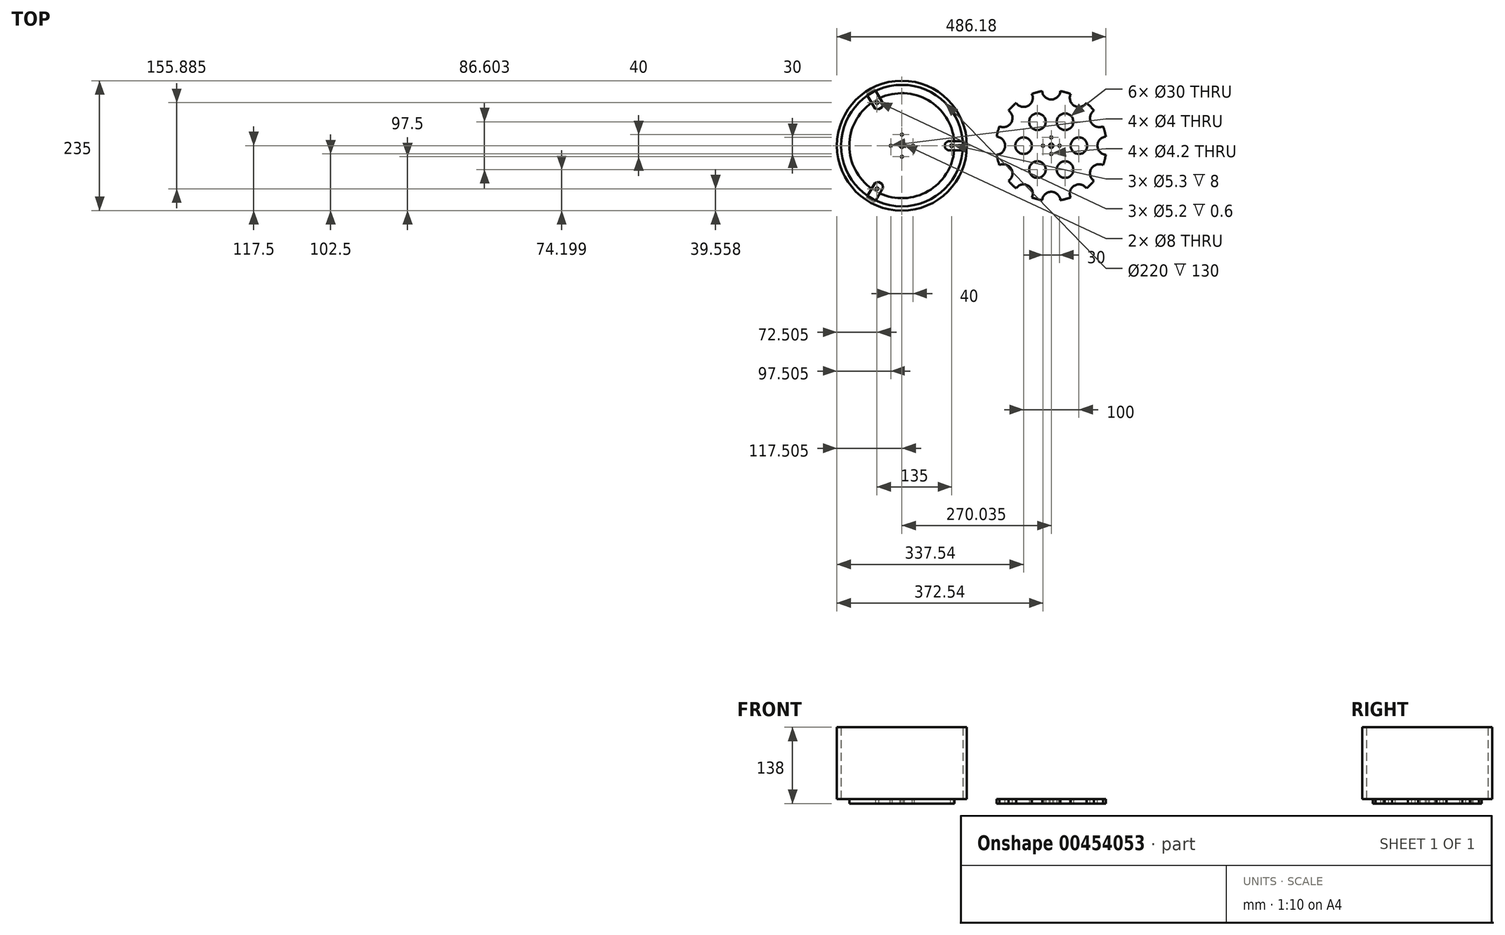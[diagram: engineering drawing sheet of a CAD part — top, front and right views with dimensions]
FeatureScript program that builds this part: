
annotation { "Feature Type Name" : "Feature", "Feature Type Description" : "" }
export const myFeature = defineFeature(function(context is Context, id is Id, definition is map)
    precondition{}
    {
        {
            var Q0;
            Q0=qCreatedBy(makeId("Top.planeOp"),FACE);
            var sketch = newSketch(context, id + "F0", { "sketchPlane" : qUnion([Q0])});
            skCircle(sketch, "E0", {"center": v(0, 0) * mm, "radius": 100 * mm});
            skCircle(sketch, "E1", {"center": v(0, 15) * mm, "radius": 2.1 * mm});
            skCircle(sketch, "E2.1.0", {"center": v(-15, 0) * mm, "radius": 2.1 * mm});
            skCircle(sketch, "E2.2.0", {"center": v(0, -15) * mm, "radius": 2.1 * mm});
            skCircle(sketch, "E2.3.0", {"center": v(15, 0) * mm, "radius": 2.1 * mm});
            skCircle(sketch, "E3", {"center": v(0, 0) * mm, "radius": 4 * mm});
            skCircle(sketch, "E4", {"center": v(-50, 0) * mm, "radius": 15 * mm});
            skCircle(sketch, "E5.1.0", {"center": v(-25, -43.3) * mm, "radius": 15 * mm});
            skCircle(sketch, "E5.2.0", {"center": v(25, -43.3) * mm, "radius": 15 * mm});
            skCircle(sketch, "E5.3.0", {"center": v(50, 0) * mm, "radius": 15 * mm});
            skCircle(sketch, "E5.4.0", {"center": v(25, 43.3) * mm, "radius": 15 * mm});
            skCircle(sketch, "E6.1.5.0", {"center": v(-25, 43.3) * mm, "radius": 15 * mm});
            skSolve(sketch);
        }
        {
            var Q0;
            Q0 = qSketchRegion(id + "F0", true);
            extrude(context, id + "F1", {"entities" : qUnion([Q0]), "depth" : 8 * mm, "offsetDistance" : 25 * mm});
        }
        {
            var Q0;
            Q0=makeQuery(id+"F1.opExtrude","CAP_FACE",FACE,{"disambiguationData":[OSD([sQuery(id+"F0.wireOp",EDGE,"E0"),sQuery(id+"F0.wireOp",EDGE,"E1"),sQuery(id+"F0.wireOp",EDGE,"E2.1.0"),sQuery(id+"F0.wireOp",EDGE,"E2.2.0"),sQuery(id+"F0.wireOp",EDGE,"E2.3.0")])],"isStart":false});
            var sketch = newSketch(context, id + "F2", { "sketchPlane" : qUnion([Q0])});
            skCircle(sketch, "E7", {"center": v(0, 100) * mm, "radius": 16.5 * mm});
            skCircle(sketch, "E8.1.0", {"center": v(-50, 86.6) * mm, "radius": 16.5 * mm});
            skCircle(sketch, "E8.2.0", {"center": v(-86.6, 50) * mm, "radius": 16.5 * mm});
            skCircle(sketch, "E8.3.0", {"center": v(-100, 0) * mm, "radius": 16.5 * mm});
            skCircle(sketch, "E8.4.0", {"center": v(-86.6, -50) * mm, "radius": 16.5 * mm});
            skCircle(sketch, "E8.5.0", {"center": v(-50, -86.6) * mm, "radius": 16.5 * mm});
            skCircle(sketch, "E8.6.0", {"center": v(0, -100) * mm, "radius": 16.5 * mm});
            skCircle(sketch, "E8.7.0", {"center": v(50, -86.6) * mm, "radius": 16.5 * mm});
            skCircle(sketch, "E8.8.0", {"center": v(86.6, -50) * mm, "radius": 16.5 * mm});
            skCircle(sketch, "E8.9.0", {"center": v(100, 0) * mm, "radius": 16.5 * mm});
            skCircle(sketch, "E8.10.0", {"center": v(86.6, 50) * mm, "radius": 16.5 * mm});
            skCircle(sketch, "E8.11.0", {"center": v(50, 86.6) * mm, "radius": 16.5 * mm});
            skPoint(sketch, "E8.center", {"position": v(0, 0) * mm});
            skSolve(sketch);
        }
        {
            var Q0;
            Q0 = qSketchRegion(id + "F2", true);
            extrude(context, id + "F3", {"entities" : qUnion([Q0]), "operationType" : NewBodyOperationType.REMOVE, "oppositeDirection" : true, "depth" : 8 * mm, "offsetDistance" : 25 * mm});
        }
        {
            var Q0;
            Q0=qCreatedBy(makeId("Top.planeOp"),FACE);
            var sketch = newSketch(context, id + "F4", { "sketchPlane" : qUnion([Q0])});
            skCircle(sketch, "E9", {"center": v(-270.04, 0) * mm, "radius": 95 * mm});
            skCircle(sketch, "E10", {"center": v(-180.04, 0) * mm, "radius": 2.65 * mm});
            skCircle(sketch, "E11.1.0", {"center": v(-315.04, 77.94) * mm, "radius": 2.65 * mm});
            skCircle(sketch, "E11.2.0", {"center": v(-315.04, -77.94) * mm, "radius": 2.65 * mm});
            skCircle(sketch, "E12", {"center": v(-270.04, 0) * mm, "radius": 4 * mm});
            skCircle(sketch, "E13", {"center": v(-270.04, 20) * mm, "radius": 2 * mm});
            skCircle(sketch, "E14.1.0", {"center": v(-290.04, 0) * mm, "radius": 2 * mm});
            skCircle(sketch, "E14.2.0", {"center": v(-270.04, -20) * mm, "radius": 2 * mm});
            skCircle(sketch, "E15.1.3.0", {"center": v(-250.04, 0) * mm, "radius": 2 * mm});
            skSolve(sketch);
        }
        {
            var Q0;
            Q0 = qSketchRegion(id + "F4", true);
            extrude(context, id + "F5", {"entities" : qUnion([Q0]), "depth" : 8 * mm, "offsetDistance" : 25 * mm});
        }
        {
            var Q0;
            Q0=makeQuery(id+"F5.opExtrude","CAP_FACE",FACE,{"disambiguationData":[OSD([sQuery(id+"F4.wireOp",EDGE,"E9"),sQuery(id+"F4.wireOp",EDGE,"E10"),sQuery(id+"F4.wireOp",EDGE,"E11.1.0"),sQuery(id+"F4.wireOp",EDGE,"E11.2.0"),sQuery(id+"F4.wireOp",EDGE,"E12"),sQuery(id+"F4.wireOp",EDGE,"E13"),sQuery(id+"F4.wireOp",EDGE,"E14.1.0"),sQuery(id+"F4.wireOp",EDGE,"E14.2.0"),sQuery(id+"F4.wireOp",EDGE,"E15.1.3.0")])],"isStart":false});
            var sketch = newSketch(context, id + "F6", { "sketchPlane" : qUnion([Q0])});
            skLineSegment(sketch, "E16.bottom", {"start": v(-191.84, -8.85) * mm, "end": v(-156.84, -8.85) * mm});
            skLineSegment(sketch, "E16.top", {"start": v(-191.84, 8.85) * mm, "end": v(-156.84, 8.85) * mm});
            skLineSegment(sketch, "E16.left", {"start": v(-191.84, -8.85) * mm, "end": v(-191.84, 8.85) * mm});
            skLineSegment(sketch, "E16.right", {"start": v(-156.84, -8.85) * mm, "end": v(-156.84, 8.85) * mm});
            skCircle(sketch, "E17", {"center": v(-180.04, 0) * mm, "radius": 2.6 * mm});
            skLineSegment(sketch, "E18.1.0", {"start": v(-301.47, 72.15) * mm, "end": v(-316.8, 63.3) * mm});
            skLineSegment(sketch, "E18.1.1", {"start": v(-316.8, 63.3) * mm, "end": v(-334.3, 93.6) * mm});
            skLineSegment(sketch, "E18.1.2", {"start": v(-301.47, 72.15) * mm, "end": v(-318.97, 102.46) * mm});
            skLineSegment(sketch, "E18.1.3", {"start": v(-318.97, 102.46) * mm, "end": v(-334.3, 93.6) * mm});
            skCircle(sketch, "E18.1.4", {"center": v(-315.04, 77.94) * mm, "radius": 2.6 * mm});
            skLineSegment(sketch, "E18.2.0", {"start": v(-316.8, -63.3) * mm, "end": v(-301.47, -72.15) * mm});
            skLineSegment(sketch, "E18.2.1", {"start": v(-301.47, -72.15) * mm, "end": v(-318.97, -102.46) * mm});
            skLineSegment(sketch, "E18.2.2", {"start": v(-316.8, -63.3) * mm, "end": v(-334.3, -93.6) * mm});
            skLineSegment(sketch, "E18.2.3", {"start": v(-334.3, -93.6) * mm, "end": v(-318.97, -102.46) * mm});
            skCircle(sketch, "E18.2.4", {"center": v(-315.04, -77.94) * mm, "radius": 2.6 * mm});
            skPoint(sketch, "E18.center", {"position": v(-270.04, 0) * mm});
            skSolve(sketch);
        }
        {
            var Q0;
            Q0 = qSketchRegion(id + "F6", true);
            extrude(context, id + "F7", {"entities" : qUnion([Q0]), "operationType" : NewBodyOperationType.ADD, "depth" : 0.6 * mm, "offsetDistance" : 25 * mm});
        }
        {
            var Q0;
            Q0=makeQuery(id+"F7.opExtrude","SWEPT_EDGE",EDGE,{"disambiguationData":[OSD([sQuery(id+"F6.wireOp",EDGE,"E16.bottom"),sQuery(id+"F6.wireOp",EDGE,"E16.left")])]});
            var Q1;
            Q1=makeQuery(id+"F7.opExtrude","SWEPT_EDGE",EDGE,{"disambiguationData":[OSD([sQuery(id+"F6.wireOp",EDGE,"E16.top"),sQuery(id+"F6.wireOp",EDGE,"E16.left")])]});
            var Q2;
            Q2=makeQuery(id+"F7.opExtrude","SWEPT_EDGE",EDGE,{"disambiguationData":[OSD([sQuery(id+"F6.wireOp",EDGE,"E18.2.0"),sQuery(id+"F6.wireOp",EDGE,"E18.2.2")])]});
            var Q3;
            Q3=makeQuery(id+"F7.opExtrude","SWEPT_EDGE",EDGE,{"disambiguationData":[OSD([sQuery(id+"F6.wireOp",EDGE,"E18.2.0"),sQuery(id+"F6.wireOp",EDGE,"E18.2.1")])]});
            var Q4;
            Q4=makeQuery(id+"F7.opExtrude","SWEPT_EDGE",EDGE,{"disambiguationData":[OSD([sQuery(id+"F6.wireOp",EDGE,"E18.1.0"),sQuery(id+"F6.wireOp",EDGE,"E18.1.1")])]});
            var Q5;
            Q5=makeQuery(id+"F7.opExtrude","SWEPT_EDGE",EDGE,{"disambiguationData":[OSD([sQuery(id+"F6.wireOp",EDGE,"E18.1.0"),sQuery(id+"F6.wireOp",EDGE,"E18.1.2")])]});
            chamfer(context, id + "F8", {"entities" : qUnion([Q0, Q1, Q2, Q3, Q4, Q5]), "width" : 5 * mm, "tangentPropagation" : true});
        }
        {
            var Q0;
            {var subQ0=sQuery(id+"F6.wireOp",EDGE,"E16.bottom");Q0=makeQuery(id+"F7.boolean.opBoolean","SPLIT",EDGE,{"disambiguationData":[topologyDisambiguationEdgeConnected([makeQuery(id+"F7.opExtrude","CAP_FACE",FACE,{"disambiguationData":[OSD([subQ0,sQuery(id+"F6.wireOp",EDGE,"E16.top"),sQuery(id+"F6.wireOp",EDGE,"E16.left"),sQuery(id+"F6.wireOp",EDGE,"E16.right"),sQuery(id+"F6.wireOp",EDGE,"E17")])],"isStart":true})])],"derivedFrom":makeQuery(id+"F7.opExtrude","CAP_EDGE",EDGE,{"disambiguationData":[OSD([subQ0])],"isStart":true})});}
            var Q1;
            {var subQ0=sQuery(id+"F6.wireOp",EDGE,"E16.top");Q1=makeQuery(id+"F7.boolean.opBoolean","SPLIT",EDGE,{"disambiguationData":[topologyDisambiguationEdgeConnected([makeQuery(id+"F7.opExtrude","CAP_FACE",FACE,{"disambiguationData":[OSD([sQuery(id+"F6.wireOp",EDGE,"E16.bottom"),subQ0,sQuery(id+"F6.wireOp",EDGE,"E16.left"),sQuery(id+"F6.wireOp",EDGE,"E16.right"),sQuery(id+"F6.wireOp",EDGE,"E17")])],"isStart":true})])],"derivedFrom":makeQuery(id+"F7.opExtrude","CAP_EDGE",EDGE,{"disambiguationData":[OSD([subQ0])],"isStart":true})});}
            var Q2;
            {var subQ0=sQuery(id+"F6.wireOp",EDGE,"E18.2.1");Q2=makeQuery(id+"F7.boolean.opBoolean","SPLIT",EDGE,{"disambiguationData":[topologyDisambiguationEdgeConnected([makeQuery(id+"F7.opExtrude","CAP_FACE",FACE,{"disambiguationData":[OSD([sQuery(id+"F6.wireOp",EDGE,"E18.2.0"),subQ0,sQuery(id+"F6.wireOp",EDGE,"E18.2.2"),sQuery(id+"F6.wireOp",EDGE,"E18.2.3"),sQuery(id+"F6.wireOp",EDGE,"E18.2.4")])],"isStart":true})])],"derivedFrom":makeQuery(id+"F7.opExtrude","CAP_EDGE",EDGE,{"disambiguationData":[OSD([subQ0])],"isStart":true})});}
            var Q3;
            {var subQ0=sQuery(id+"F6.wireOp",EDGE,"E18.2.2");Q3=makeQuery(id+"F7.boolean.opBoolean","SPLIT",EDGE,{"disambiguationData":[topologyDisambiguationEdgeConnected([makeQuery(id+"F7.opExtrude","CAP_FACE",FACE,{"disambiguationData":[OSD([sQuery(id+"F6.wireOp",EDGE,"E18.2.0"),sQuery(id+"F6.wireOp",EDGE,"E18.2.1"),subQ0,sQuery(id+"F6.wireOp",EDGE,"E18.2.3"),sQuery(id+"F6.wireOp",EDGE,"E18.2.4")])],"isStart":true})])],"derivedFrom":makeQuery(id+"F7.opExtrude","CAP_EDGE",EDGE,{"disambiguationData":[OSD([subQ0])],"isStart":true})});}
            var Q4;
            {var subQ0=sQuery(id+"F6.wireOp",EDGE,"E18.1.1");Q4=makeQuery(id+"F7.boolean.opBoolean","SPLIT",EDGE,{"disambiguationData":[topologyDisambiguationEdgeConnected([makeQuery(id+"F7.opExtrude","CAP_FACE",FACE,{"disambiguationData":[OSD([sQuery(id+"F6.wireOp",EDGE,"E18.1.0"),subQ0,sQuery(id+"F6.wireOp",EDGE,"E18.1.2"),sQuery(id+"F6.wireOp",EDGE,"E18.1.3"),sQuery(id+"F6.wireOp",EDGE,"E18.1.4")])],"isStart":true})])],"derivedFrom":makeQuery(id+"F7.opExtrude","CAP_EDGE",EDGE,{"disambiguationData":[OSD([subQ0])],"isStart":true})});}
            var Q5;
            {var subQ0=sQuery(id+"F6.wireOp",EDGE,"E18.1.2");Q5=makeQuery(id+"F7.boolean.opBoolean","SPLIT",EDGE,{"disambiguationData":[topologyDisambiguationEdgeConnected([makeQuery(id+"F7.opExtrude","CAP_FACE",FACE,{"disambiguationData":[OSD([sQuery(id+"F6.wireOp",EDGE,"E18.1.0"),sQuery(id+"F6.wireOp",EDGE,"E18.1.1"),subQ0,sQuery(id+"F6.wireOp",EDGE,"E18.1.3"),sQuery(id+"F6.wireOp",EDGE,"E18.1.4")])],"isStart":true})])],"derivedFrom":makeQuery(id+"F7.opExtrude","CAP_EDGE",EDGE,{"disambiguationData":[OSD([subQ0])],"isStart":true})});}
            chamfer(context, id + "F9", {"entities" : qUnion([Q0, Q1, Q2, Q3, Q4, Q5]), "width" : 1 * mm, "tangentPropagation" : true});
        }
        {
            var Q0;
            Q0=makeQuery(id+"F5.opExtrude","CAP_FACE",FACE,{"disambiguationData":[OSD([sQuery(id+"F4.wireOp",EDGE,"E9"),sQuery(id+"F4.wireOp",EDGE,"E10"),sQuery(id+"F4.wireOp",EDGE,"E11.1.0"),sQuery(id+"F4.wireOp",EDGE,"E11.2.0"),sQuery(id+"F4.wireOp",EDGE,"E12"),sQuery(id+"F4.wireOp",EDGE,"E13"),sQuery(id+"F4.wireOp",EDGE,"E14.1.0"),sQuery(id+"F4.wireOp",EDGE,"E14.2.0"),sQuery(id+"F4.wireOp",EDGE,"E15.1.3.0")])],"isStart":false});
            var sketch = newSketch(context, id + "F10", { "sketchPlane" : qUnion([Q0])});
            skCircle(sketch, "E19", {"center": v(-270.04, 0) * mm, "radius": 117.5 * mm});
            skCircle(sketch, "E20", {"center": v(-270.04, 0) * mm, "radius": 110 * mm});
            skSolve(sketch);
        }
        {
            var Q0;
            Q0 = qSketchRegion(id + "F10", true);
            extrude(context, id + "F11", {"entities" : qUnion([Q0]), "depth" : 130 * mm, "offsetDistance" : 25 * mm});
        }
    });
